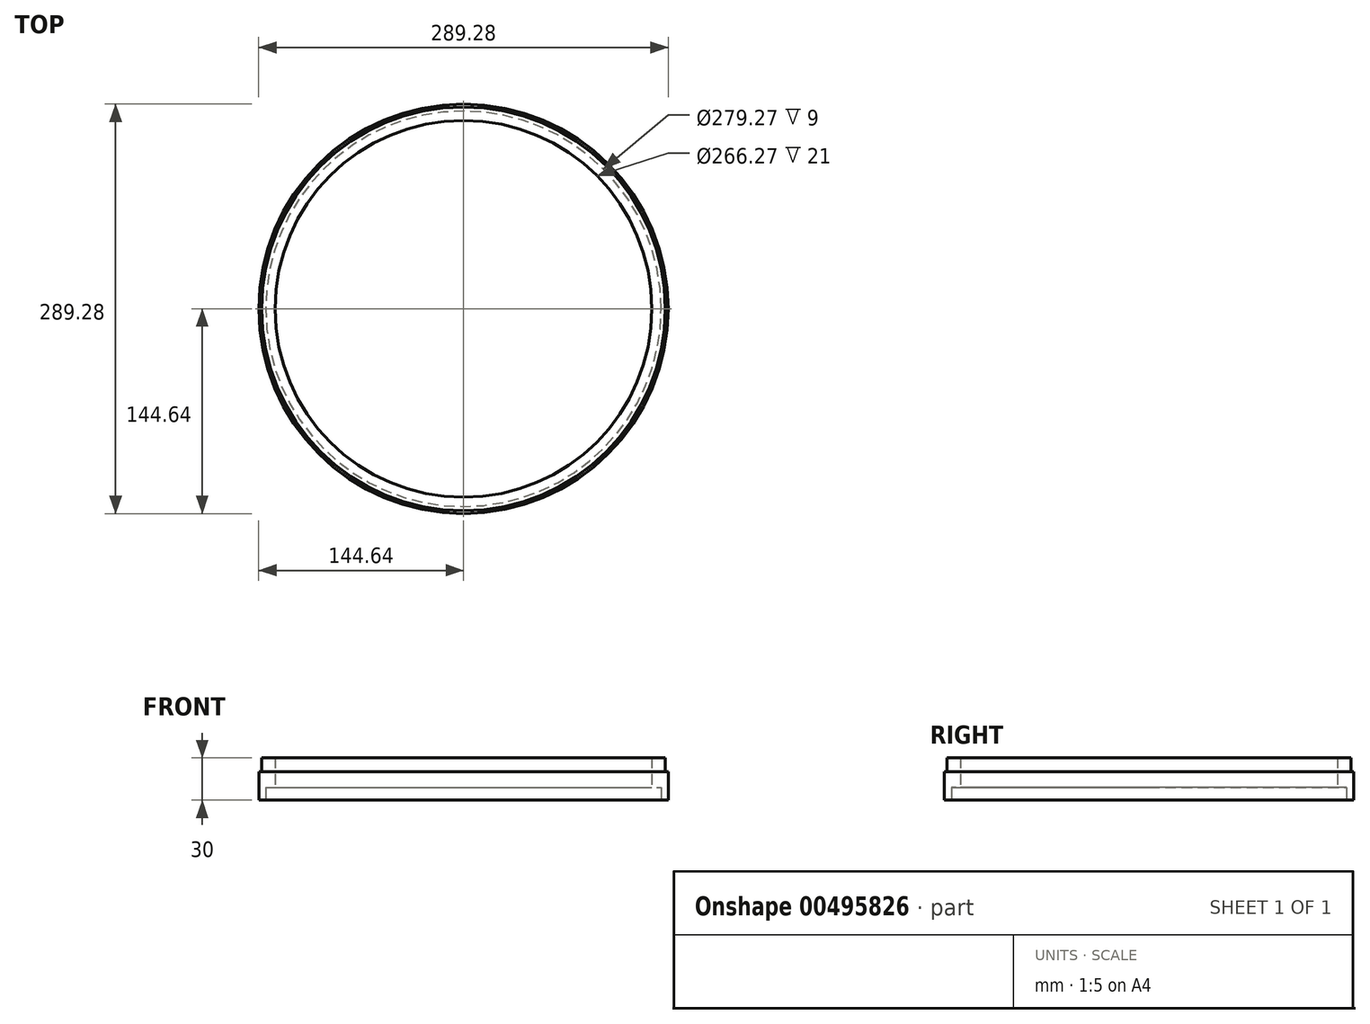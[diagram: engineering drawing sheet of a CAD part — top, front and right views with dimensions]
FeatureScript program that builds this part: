
annotation { "Feature Type Name" : "Feature", "Feature Type Description" : "" }
export const myFeature = defineFeature(function(context is Context, id is Id, definition is map)
    precondition{}
    {
        {
            var Q0;
            Q0=qCreatedBy(makeId("Front.planeOp"),FACE);
            var sketch = newSketch(context, id + "F0", { "sketchPlane" : qUnion([Q0])});
            skLineSegment(sketch, "E0", {"start": v(-144.64, 0) * mm, "end": v(-144.64, 20) * mm});
            skLineSegment(sketch, "E1", {"start": v(-144.64, 20) * mm, "end": v(-142.64, 20) * mm});
            skLineSegment(sketch, "E2", {"start": v(-142.64, 20) * mm, "end": v(-142.64, 30) * mm});
            skLineSegment(sketch, "E3", {"start": v(-142.64, 30) * mm, "end": v(-133.14, 30) * mm});
            skLineSegment(sketch, "E4", {"start": v(-133.14, 30) * mm, "end": v(-133.14, 9) * mm});
            skLineSegment(sketch, "E5", {"start": v(-133.14, 9) * mm, "end": v(-139.64, 9) * mm});
            skLineSegment(sketch, "E6", {"start": v(-139.64, 9) * mm, "end": v(-139.64, 0) * mm});
            skLineSegment(sketch, "E7", {"start": v(-139.64, 0) * mm, "end": v(-144.64, 0) * mm});
            skPoint(sketch, "E8.positionSnap0", {"position": v(-142.14, 0) * mm});
            skLineSegment(sketch, "E9", {"start": v(0, 0) * mm, "end": v(0, 32.71) * mm});
            skSolve(sketch);
        }
        {
            var Q0;
            Q0 = qSketchRegion(id + "F0", true);
            var Q1;
            Q1=sQuery(id+"F0.wireOp",EDGE,"E9");
            revolve(context, id + "F1", {"entities" : qUnion([Q0]), "axis" : qUnion([Q1]), "revolveType" : RevolveType.FULL});
        }
    });
